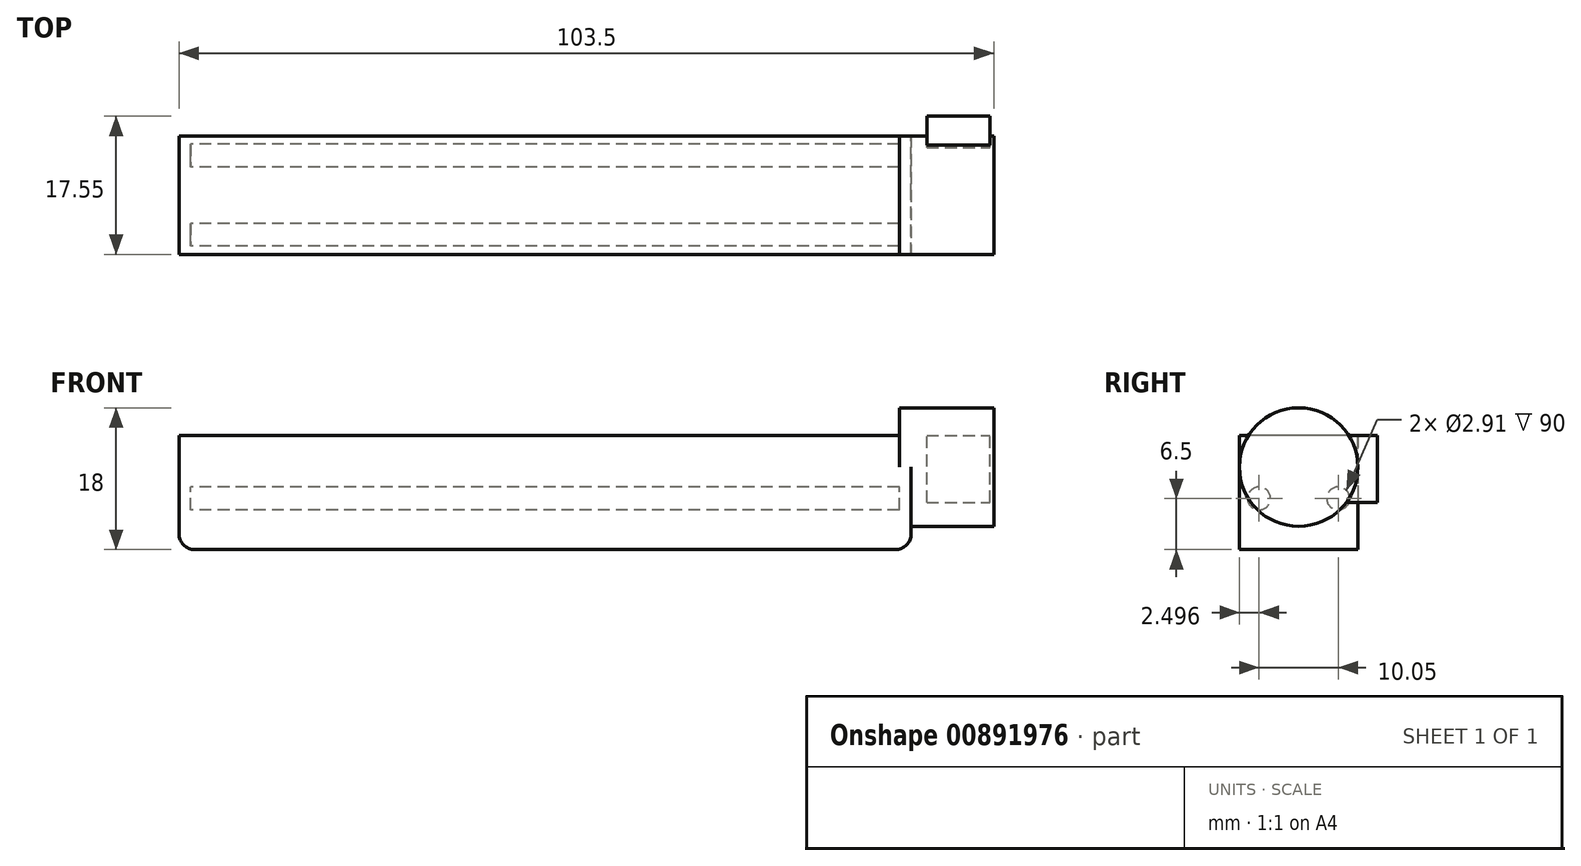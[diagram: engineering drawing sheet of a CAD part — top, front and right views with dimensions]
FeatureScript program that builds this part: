
annotation { "Feature Type Name" : "Feature", "Feature Type Description" : "" }
export const myFeature = defineFeature(function(context is Context, id is Id, definition is map)
    precondition{}
    {
        {
            var Q0;
            Q0=qCreatedBy(makeId("Top.planeOp"),FACE);
            var sketch = newSketch(context, id + "F0", { "sketchPlane" : qUnion([Q0])});
            skLineSegment(sketch, "E0.bottom", {"start": v(-46.5, -1.3) * mm, "end": v(46.5, -1.3) * mm});
            skLineSegment(sketch, "E0.top", {"start": v(-46.5, -16.34) * mm, "end": v(46.5, -16.34) * mm});
            skLineSegment(sketch, "E0.left", {"start": v(-46.5, -1.3) * mm, "end": v(-46.5, -16.34) * mm});
            skLineSegment(sketch, "E0.right", {"start": v(46.5, -1.3) * mm, "end": v(46.5, -16.34) * mm});
            skSolve(sketch);
        }
        {
            var Q0;
            Q0 = qSketchRegion(id + "F0", true);
            var Q1;
            Q1 = qSketchRegion(id + "F2", true);
            extrude(context, id + "F1", {"entities" : qUnion([Q0, Q1]), "depth" : 1.5 * mm, "offsetDistance" : 25 * mm});
        }
        {
            var Q0;
            Q0=makeQuery(id+"F1.opExtrude","SWEPT_FACE",FACE,{"disambiguationData":[OSD([sQuery(id+"F0.wireOp",EDGE,"E0.left")])]});
            var sketch = newSketch(context, id + "F2", { "sketchPlane" : qUnion([Q0])});
            skLineSegment(sketch, "E1.bottom", {"start": v(1.3, 0) * mm, "end": v(16.34, 0) * mm});
            skLineSegment(sketch, "E1.top", {"start": v(1.3, 14.5) * mm, "end": v(16.34, 14.5) * mm});
            skLineSegment(sketch, "E1.left", {"start": v(1.3, 0) * mm, "end": v(1.3, 14.5) * mm});
            skLineSegment(sketch, "E1.right", {"start": v(16.34, 0) * mm, "end": v(16.34, 14.5) * mm});
            skSolve(sketch);
        }
        {
            var Q0;
            {var subQ0=sQuery(id+"F2.wireOp",EDGE,"E1.top");Q0=makeQuery(id+"F2.imprint","IMPRINT",FACE,{"disambiguationData":[TD([[makeQuery(id+"F2.imprint","IMPRINT",EDGE,{"derivedFrom":subQ0}),-1.0]])]});}
            extrude(context, id + "F3", {"entities" : qUnion([Q0]), "operationType" : NewBodyOperationType.ADD, "oppositeDirection" : true, "depth" : 1.5 * mm, "offsetDistance" : 25 * mm});
        }
        {
            var Q0;
            Q0=makeQuery(id+"F1.opExtrude","CAP_EDGE",EDGE,{"disambiguationData":[OSD([sQuery(id+"F0.wireOp",EDGE,"E0.left")])],"isStart":true});
            fillet(context, id + "F4", {"entities" : qUnion([Q0]), "radius" : 2 * mm, "tangentPropagation" : true, "allowEdgeOverflow" : false});
        }
        {
            var Q0;
            Q0=makeQuery(id+"F1.opExtrude","SWEPT_FACE",FACE,{"disambiguationData":[OSD([sQuery(id+"F0.wireOp",EDGE,"E0.right")])]});
            var Q1;
            Q1=makeQuery(id+"F1.opExtrude","SWEPT_FACE",FACE,{"disambiguationData":[OSD([sQuery(id+"F0.wireOp",EDGE,"E0.right")])]});
            var sketch = newSketch(context, id + "F5", { "sketchPlane" : qUnion([Q0, Q1])});
            skLineSegment(sketch, "E2.bottom", {"start": v(-16.34, 0) * mm, "end": v(-1.3, 0) * mm});
            skLineSegment(sketch, "E2.top", {"start": v(-16.34, 10.47) * mm, "end": v(-1.3, 10.47) * mm});
            skLineSegment(sketch, "E2.left", {"start": v(-16.34, 0) * mm, "end": v(-16.34, 10.47) * mm});
            skLineSegment(sketch, "E2.right", {"start": v(-1.3, 0) * mm, "end": v(-1.3, 10.47) * mm});
            skCircle(sketch, "E3", {"center": v(-8.82, 10.47) * mm, "radius": 7.53 * mm});
            skSolve(sketch);
        }
        {
            var Q0;
            Q0 = qSketchRegion(id + "F5", true);
            extrude(context, id + "F6", {"entities" : qUnion([Q0]), "operationType" : NewBodyOperationType.ADD, "oppositeDirection" : true, "depth" : 1.5 * mm, "offsetDistance" : 25 * mm});
        }
        {
            var Q0;
            Q0=makeQuery(id+"F1.opExtrude","CAP_EDGE",EDGE,{"disambiguationData":[OSD([sQuery(id+"F0.wireOp",EDGE,"E0.right")])],"isStart":true});
            fillet(context, id + "F7", {"entities" : qUnion([Q0]), "radius" : 2 * mm, "tangentPropagation" : true, "allowEdgeOverflow" : false});
        }
        {
            var Q0;
            Q0=makeQuery(id+"F6.boolean.opBoolean","MERGE",FACE,{"derivedFrom":[makeQuery(id+"F1.opExtrude","SWEPT_FACE",FACE,{"disambiguationData":[OSD([sQuery(id+"F0.wireOp",EDGE,"E0.right")])]}),makeQuery(id+"F6.opExtrude","CAP_FACE",FACE,{"disambiguationData":[OSD([sQuery(id+"F5.wireOp",EDGE,"E2.bottom"),sQuery(id+"F5.wireOp",EDGE,"E2.left"),sQuery(id+"F5.wireOp",EDGE,"E2.right"),sQuery(id+"F5.wireOp",EDGE,"E3")])],"isStart":true})]});
            var sketch = newSketch(context, id + "F8", { "sketchPlane" : qUnion([Q0])});
            skLineSegment(sketch, "E4", {"start": v(-16.34, 10.47) * mm, "end": v(-1.3, 10.47) * mm});
            skCircle(sketch, "E5", {"center": v(-8.82, 10.47) * mm, "radius": 1.5 * mm});
            skSolve(sketch);
        }
        {
            var Q0;
            Q0 = qSketchRegion(id + "F8", true);
            extrude(context, id + "F9", {"entities" : qUnion([Q0]), "operationType" : NewBodyOperationType.ADD, "oppositeDirection" : true, "depth" : 93 * mm, "offsetDistance" : 25 * mm});
        }
        {
            var Q0;
            Q0=makeQuery(id+"F6.boolean.opBoolean","MERGE",FACE,{"derivedFrom":[makeQuery(id+"F1.opExtrude","SWEPT_FACE",FACE,{"disambiguationData":[OSD([sQuery(id+"F0.wireOp",EDGE,"E0.right")])]}),makeQuery(id+"F6.opExtrude","CAP_FACE",FACE,{"disambiguationData":[OSD([sQuery(id+"F5.wireOp",EDGE,"E2.bottom"),sQuery(id+"F5.wireOp",EDGE,"E2.left"),sQuery(id+"F5.wireOp",EDGE,"E2.right"),sQuery(id+"F5.wireOp",EDGE,"E3")])],"isStart":true})]});
            var sketch = newSketch(context, id + "F10", { "sketchPlane" : qUnion([Q0])});
            skLineSegment(sketch, "E6", {"start": v(-16.34, 10.47) * mm, "end": v(-1.3, 10.47) * mm});
            skCircle(sketch, "E7", {"center": v(-8.82, 10.47) * mm, "radius": 7.53 * mm});
            skSolve(sketch);
        }
        {
            var Q0;
            Q0 = qSketchRegion(id + "F10", true);
            extrude(context, id + "F11", {"entities" : qUnion([Q0]), "operationType" : NewBodyOperationType.ADD, "depth" : 10.5 * mm, "offsetDistance" : 25 * mm});
        }
        {
            var Q0;
            Q0=makeQuery(id+"F3.opExtrude","CAP_FACE",FACE,{"disambiguationData":[OSD([sQuery(id+"F0.wireOp",EDGE,"E0.left"),sQuery(id+"F2.wireOp",EDGE,"E1.top"),sQuery(id+"F2.wireOp",EDGE,"E1.left"),sQuery(id+"F2.wireOp",EDGE,"E1.right")])],"isStart":false});
            var sketch = newSketch(context, id + "F12", { "sketchPlane" : qUnion([Q0])});
            skLineSegment(sketch, "E8.bottom", {"start": v(-16.34, 1.5) * mm, "end": v(-1.3, 1.5) * mm});
            skLineSegment(sketch, "E8.top", {"start": v(-16.34, 6.5) * mm, "end": v(-1.3, 6.5) * mm});
            skLineSegment(sketch, "E8.left", {"start": v(-16.34, 1.5) * mm, "end": v(-16.34, 6.5) * mm});
            skLineSegment(sketch, "E8.right", {"start": v(-1.3, 1.5) * mm, "end": v(-1.3, 6.5) * mm});
            skLineSegment(sketch, "E9", {"start": v(-16.34, 6.5) * mm, "end": v(-13.84, 6.5) * mm});
            skLineSegment(sketch, "E10", {"start": v(-1.3, 6.5) * mm, "end": v(-3.8, 6.5) * mm});
            skCircle(sketch, "E11", {"center": v(-13.84, 6.5) * mm, "radius": 1.46 * mm});
            skCircle(sketch, "E12", {"center": v(-3.8, 6.5) * mm, "radius": 1.46 * mm});
            skSolve(sketch);
        }
        {
            var Q0;
            {var subQ0=sQuery(id+"F12.wireOp",EDGE,"E9");var subQ1=sQuery(id+"F12.wireOp",EDGE,"E8.top");var subQ2=makeQuery(id+"F12.imprint","INTERSECT",VERTEX,{"derivedFrom":[subQ1,subQ0]});Q0=makeQuery(id+"F12.imprint","IMPRINT",FACE,{"disambiguationData":[TD([[makeQuery(id+"F12.imprint","IMPRINT",EDGE,{"disambiguationData":[TD([[subQ2,-1.0]])],"derivedFrom":subQ1}),1.0]])]});}
            var Q1;
            {var subQ0=sQuery(id+"F12.wireOp",EDGE,"E9");var subQ1=sQuery(id+"F12.wireOp",EDGE,"E8.top");var subQ2=makeQuery(id+"F12.imprint","INTERSECT",VERTEX,{"derivedFrom":[subQ1,subQ0]});Q1=makeQuery(id+"F12.imprint","IMPRINT",FACE,{"disambiguationData":[TD([[makeQuery(id+"F12.imprint","IMPRINT",EDGE,{"disambiguationData":[TD([[subQ2,-1.0]])],"derivedFrom":subQ1}),-1.0]])]});}
            var Q2;
            {var subQ0=sQuery(id+"F12.wireOp",EDGE,"E10");var subQ1=sQuery(id+"F12.wireOp",EDGE,"E8.top");var subQ2=makeQuery(id+"F12.imprint","INTERSECT",VERTEX,{"derivedFrom":[subQ1,subQ0]});Q2=makeQuery(id+"F12.imprint","IMPRINT",FACE,{"disambiguationData":[TD([[makeQuery(id+"F12.imprint","IMPRINT",EDGE,{"disambiguationData":[TD([[subQ2,1.0]])],"derivedFrom":subQ1}),-1.0]])]});}
            var Q3;
            {var subQ0=sQuery(id+"F12.wireOp",EDGE,"E10");var subQ1=sQuery(id+"F12.wireOp",EDGE,"E8.top");var subQ2=makeQuery(id+"F12.imprint","INTERSECT",VERTEX,{"derivedFrom":[subQ1,subQ0]});Q3=makeQuery(id+"F12.imprint","IMPRINT",FACE,{"disambiguationData":[TD([[makeQuery(id+"F12.imprint","IMPRINT",EDGE,{"disambiguationData":[TD([[subQ2,1.0]])],"derivedFrom":subQ1}),1.0]])]});}
            var Q4;
            Q4=makeQuery(id+"F6.opExtrude","CAP_FACE",FACE,{"disambiguationData":[OSD([sQuery(id+"F5.wireOp",EDGE,"E2.bottom"),sQuery(id+"F5.wireOp",EDGE,"E2.left"),sQuery(id+"F5.wireOp",EDGE,"E2.right"),sQuery(id+"F5.wireOp",EDGE,"E3")])],"isStart":false});
            extrude(context, id + "F13", {"entities" : qUnion([Q0, Q1, Q2, Q3]), "operationType" : NewBodyOperationType.ADD, "endBound" : BoundingType.UP_TO_SURFACE, "depth" : 25 * mm, "endBoundEntityFace" : qUnion([Q4]), "offsetDistance" : 25 * mm});
        }
        {
            var Q0;
            Q0=makeQuery(id+"F6.boolean.opBoolean","MERGE",FACE,{"derivedFrom":[makeQuery(id+"F3.boolean.opBoolean","MERGE",FACE,{"derivedFrom":[makeQuery(id+"F1.opExtrude","SWEPT_FACE",FACE,{"disambiguationData":[OSD([sQuery(id+"F0.wireOp",EDGE,"E0.bottom")])]}),makeQuery(id+"F3.opExtrude","SWEPT_FACE",FACE,{"disambiguationData":[OSD([sQuery(id+"F2.wireOp",EDGE,"E1.left")])]})]}),makeQuery(id+"F6.opExtrude","SWEPT_FACE",FACE,{"disambiguationData":[OSD([sQuery(id+"F5.wireOp",EDGE,"E2.right")])]})]});
            cPlane(context, id + "F14", {"entities" : qUnion([Q0]), "cplaneType" : CPlaneType.OFFSET, "offset" : 0 * mm, "width" : 150 * mm, "height" : 150 * mm});
        }
        {
            var Q0;
            Q0=qCreatedBy(id+"F14.planeOp",FACE);
            var sketch = newSketch(context, id + "F15", { "sketchPlane" : qUnion([Q0])});
            skPoint(sketch, "E13.0", {"position": v(-45, 5.99) * mm});
            skLineSegment(sketch, "E14", {"start": v(-48.5, 5.99) * mm, "end": v(-45, 5.99) * mm});
            skLineSegment(sketch, "E15.bottom", {"start": v(-48.5, 5.99) * mm, "end": v(-56.5, 5.99) * mm});
            skLineSegment(sketch, "E15.top", {"start": v(-48.5, 14.49) * mm, "end": v(-56.5, 14.49) * mm});
            skLineSegment(sketch, "E15.left", {"start": v(-48.5, 5.99) * mm, "end": v(-48.5, 14.49) * mm});
            skLineSegment(sketch, "E15.right", {"start": v(-56.5, 5.99) * mm, "end": v(-56.5, 14.49) * mm});
            skSolve(sketch);
        }
        {
            var Q0;
            Q0=makeQuery(id+"F15.imprint","IMPRINT",FACE,{"disambiguationData":[TD([[makeQuery(id+"F15.imprint","IMPRINT",EDGE,{"derivedFrom":sQuery(id+"F15.wireOp",EDGE,"E15.bottom")}),-1.0]])]});
            extrude(context, id + "F16", {"entities" : qUnion([Q0]), "operationType" : NewBodyOperationType.ADD, "depth" : 2.5 * mm, "offsetDistance" : 25 * mm, "hasSecondDirection" : true, "secondDirectionOppositeDirection" : true, "secondDirectionDepth" : 2.5 * mm});
        }
    });
